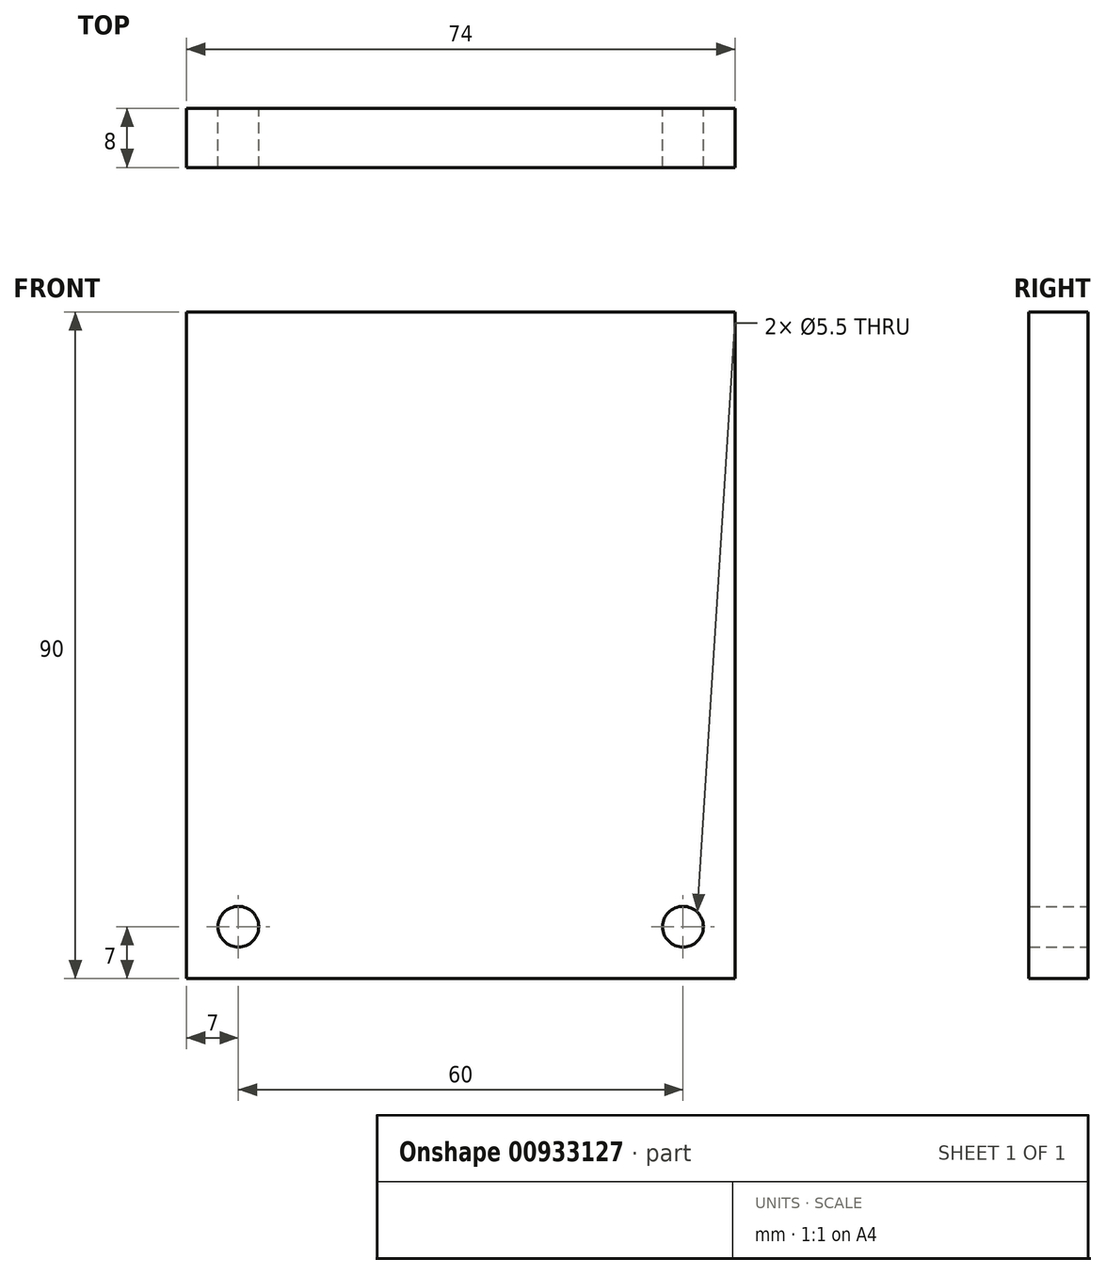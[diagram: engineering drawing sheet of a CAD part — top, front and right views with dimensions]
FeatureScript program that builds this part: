
annotation { "Feature Type Name" : "Feature", "Feature Type Description" : "" }
export const myFeature = defineFeature(function(context is Context, id is Id, definition is map)
    precondition{}
    {
        {
            var Q0;
            Q0=qCreatedBy(makeId("Front.planeOp"),FACE);
            var sketch = newSketch(context, id + "F0", { "sketchPlane" : qUnion([Q0])});
            skLineSegment(sketch, "E0.top", {"start": v(37, -45) * mm, "end": v(-37, -45) * mm});
            skLineSegment(sketch, "E0.left", {"start": v(37, 45) * mm, "end": v(37, -45) * mm});
            skLineSegment(sketch, "E0.right", {"start": v(-37, 45) * mm, "end": v(-37, -45) * mm});
            skPoint(sketch, "E0.middle", {"position": v(0, 0) * mm});
            skCircle(sketch, "E1", {"center": v(30, -38) * mm, "radius": 2.75 * mm});
            skCircle(sketch, "E2.MirrorC", {"center": v(-30, -38) * mm, "radius": 2.75 * mm});
            skLineSegment(sketch, "E3", {"start": v(-37, 45) * mm, "end": v(37, 45) * mm});
            skSolve(sketch);
        }
        {
            var Q0;
            Q0 = qSketchRegion(id + "F0", true);
            extrude(context, id + "F1", {"entities" : qUnion([Q0]), "depth" : 8 * mm, "offsetDistance" : 25 * mm});
        }
    });
